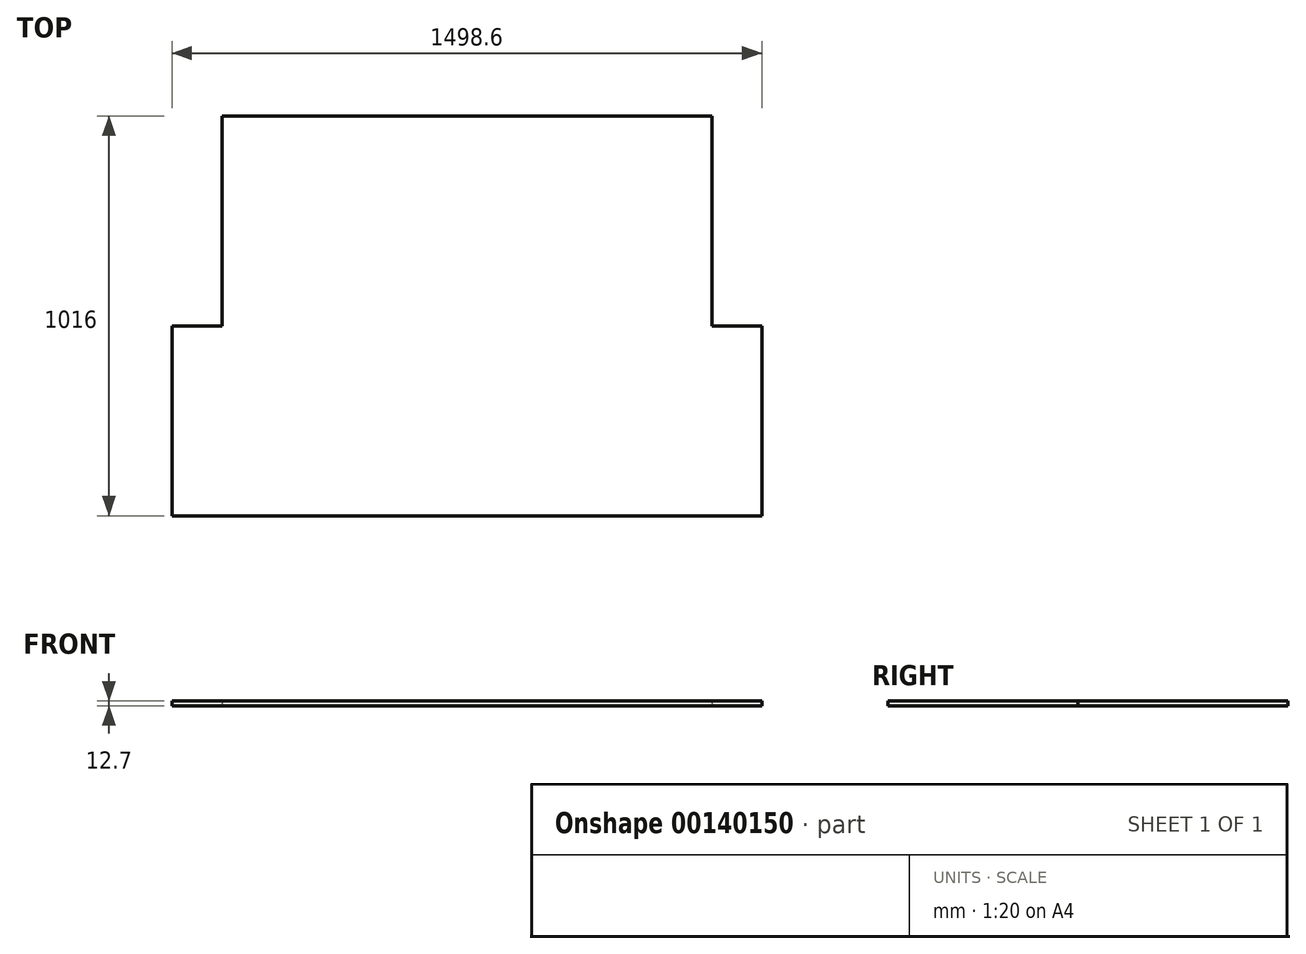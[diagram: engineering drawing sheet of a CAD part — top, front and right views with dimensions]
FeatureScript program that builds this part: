
annotation { "Feature Type Name" : "Feature", "Feature Type Description" : "" }
export const myFeature = defineFeature(function(context is Context, id is Id, definition is map)
    precondition{}
    {
        {
            var Q0;
            Q0=qCreatedBy(makeId("Front.planeOp"),FACE);
            var sketch = newSketch(context, id + "F0", { "sketchPlane" : qUnion([Q0])});
            skLineSegment(sketch, "E0", {"start": v(0, 0) * mm, "end": v(-749.3, 0) * mm});
            skLineSegment(sketch, "E1", {"start": v(0, 0) * mm, "end": v(749.3, 0) * mm});
            skLineSegment(sketch, "E2", {"start": v(-749.3, 0) * mm, "end": v(-749.3, 12.7) * mm});
            skLineSegment(sketch, "E3", {"start": v(749.3, 12.7) * mm, "end": v(749.3, 0) * mm});
            skLineSegment(sketch, "E4", {"start": v(749.3, 12.7) * mm, "end": v(-749.3, 12.7) * mm});
            skLineSegment(sketch, "E5", {"start": v(-622.3, 12.7) * mm, "end": v(-622.3, 0) * mm});
            skLineSegment(sketch, "E6", {"start": v(622.3, 12.7) * mm, "end": v(622.3, 0) * mm});
            skSolve(sketch);
        }
        {
            var Q0;
            {var subQ0=sQuery(id+"F0.wireOp",EDGE,"E2");Q0=makeQuery(id+"F0.imprint","IMPRINT",FACE,{"disambiguationData":[TD([[makeQuery(id+"F0.imprint","IMPRINT",EDGE,{"derivedFrom":subQ0}),-1.0]])]});}
            var Q1;
            {var subQ0=sQuery(id+"F0.wireOp",EDGE,"E5");Q1=makeQuery(id+"F0.imprint","IMPRINT",FACE,{"disambiguationData":[TD([[makeQuery(id+"F0.imprint","IMPRINT",EDGE,{"derivedFrom":subQ0}),1.0]])]});}
            var Q2;
            {var subQ0=sQuery(id+"F0.wireOp",EDGE,"E3");Q2=makeQuery(id+"F0.imprint","IMPRINT",FACE,{"disambiguationData":[TD([[makeQuery(id+"F0.imprint","IMPRINT",EDGE,{"derivedFrom":subQ0}),-1.0]])]});}
            extrude(context, id + "F1", {"entities" : qUnion([Q0, Q1, Q2]), "depth" : 1016 * mm});
        }
        {
            var Q0;
            {var subQ0=sQuery(id+"F0.wireOp",EDGE,"E2");Q0=makeQuery(id+"F0.imprint","IMPRINT",FACE,{"disambiguationData":[TD([[makeQuery(id+"F0.imprint","IMPRINT",EDGE,{"derivedFrom":subQ0}),-1.0]])]});}
            var Q1;
            {var subQ0=sQuery(id+"F0.wireOp",EDGE,"E3");Q1=makeQuery(id+"F0.imprint","IMPRINT",FACE,{"disambiguationData":[TD([[makeQuery(id+"F0.imprint","IMPRINT",EDGE,{"derivedFrom":subQ0}),-1.0]])]});}
            extrude(context, id + "F2", {"entities" : qUnion([Q0, Q1]), "operationType" : NewBodyOperationType.REMOVE, "depth" : 533.4 * mm});
        }
    });
